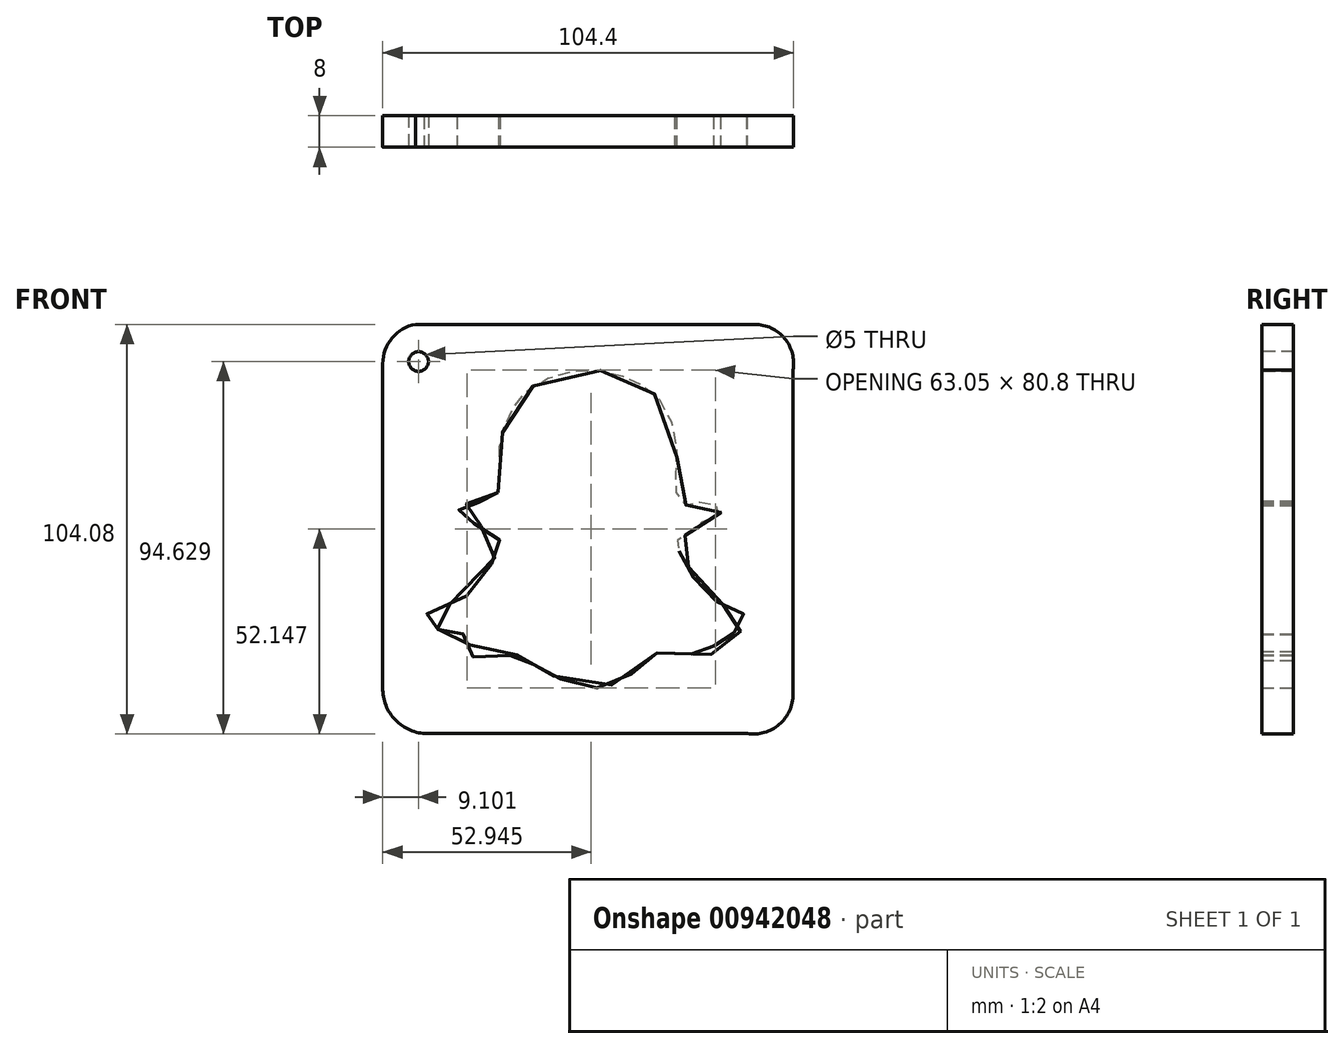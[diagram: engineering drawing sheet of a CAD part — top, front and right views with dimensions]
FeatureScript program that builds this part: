
annotation { "Feature Type Name" : "Feature", "Feature Type Description" : "" }
export const myFeature = defineFeature(function(context is Context, id is Id, definition is map)
    precondition{}
    {
        {
            var Q0;
            Q0=qCreatedBy(makeId("Front.planeOp"),FACE);
            var sketch = newSketch(context, id + "F0", { "sketchPlane" : qUnion([Q0])});
            skFitSpline(sketch, "E0", {"points": [v(-22.56, 0) * mm, v(-22.27, 10.78) * mm, v(-19.69, 19.69) * mm, v(-13.94, 26.87) * mm, v(0, 31.18) * mm, v(10.78, 28.88) * mm, v(18.83, 23.14) * mm, v(22.85, 9.63) * mm, v(22.56, 0) * mm, v(25.72, -3.3) * mm, v(30.32, -2.16) * mm, v(34.06, -5.03) * mm, v(29.17, -7.62) * mm, v(25.15, -10.78) * mm, v(22.56, -12.79) * mm, v(24.57, -16.53) * mm, v(27.73, -22.85) * mm, v(34.06, -28.3) * mm, v(39.8, -30.9) * mm, v(39.8, -34.92) * mm, v(32.62, -36.64) * mm, v(32.05, -40.67) * mm, v(24, -40.67) * mm, v(16.81, -41.24) * mm, v(10.2, -47) * mm, v(0, -49.58) * mm, v(-9.34, -46.13) * mm, v(-14.23, -43.26) * mm, v(-17.96, -41.24) * mm, v(-28.6, -42.1) * mm, v(-30.32, -36.36) * mm, v(-34.63, -36.07) * mm, v(-39.23, -33.77) * mm, v(-41.24, -31.47) * mm, v(-30.6, -26.3) * mm, v(-23.71, -17.1) * mm, v(-21.99, -12.79) * mm, v(-25.44, -9.05) * mm, v(-32.62, -6.18) * mm, v(-32.33, -4.17) * mm, v(-28.88, -2.44) * mm, v(-26.3, -2.73) * mm, v(-22.56, 0) * mm]});
            skLineSegment(sketch, "E1", {"start": v(-51.89, 32.7) * mm, "end": v(-51.89, -49.62) * mm});
            skLineSegment(sketch, "E2", {"start": v(-40.52, -61.26) * mm, "end": v(40.71, -61.26) * mm});
            skLineSegment(sketch, "E3", {"start": v(52.35, -51.24) * mm, "end": v(52.35, 31.07) * mm});
            skLineSegment(sketch, "E4", {"start": v(42.6, 42.71) * mm, "end": v(-37.27, 42.71) * mm});
            skArc(sketch, "E5", {"start": v(-51.89, -49.62) * mm, "mid": v(-48.65, -57.83) * mm, "end": v(-40.52, -61.26) * mm});
            skArc(sketch, "E6", {"start": v(52.35, 31.07) * mm, "mid": v(50.2, 39.17) * mm, "end": v(42.6, 42.71) * mm});
            skArc(sketch, "E7", {"start": v(-43.53, 42.71) * mm, "mid": v(-49.52, 39.22) * mm, "end": v(-51.89, 32.7) * mm});
            skArc(sketch, "E8", {"start": v(40.71, -61.26) * mm, "mid": v(48.83, -58.92) * mm, "end": v(52.35, -51.24) * mm});
            skLineSegment(sketch, "E9", {"start": v(-43.53, 42.71) * mm, "end": v(-37.27, 42.71) * mm});
            skSolve(sketch);
        }
        {
            var Q0;
            Q0 = qSketchRegion(id + "F0", true);
            extrude(context, id + "F1", {"entities" : qUnion([Q0]), "depth" : 8 * mm, "offsetDistance" : 25 * mm});
        }
        {
            var Q0;
            Q0=makeQuery(id+"F1.opExtrude","CAP_FACE",FACE,{"disambiguationData":[OSD([sQuery(id+"F0.wireOp",EDGE,"E0"),sQuery(id+"F0.wireOp",EDGE,"E1"),sQuery(id+"F0.wireOp",EDGE,"E2"),sQuery(id+"F0.wireOp",EDGE,"E3"),sQuery(id+"F0.wireOp",EDGE,"E4"),sQuery(id+"F0.wireOp",EDGE,"E5"),sQuery(id+"F0.wireOp",EDGE,"E6"),sQuery(id+"F0.wireOp",EDGE,"E7"),sQuery(id+"F0.wireOp",EDGE,"E8"),sQuery(id+"F0.wireOp",EDGE,"E9")])],"isStart":false});
            var sketch = newSketch(context, id + "F2", { "sketchPlane" : qUnion([Q0])});
            skCircle(sketch, "E10", {"center": v(-42.79, 33.26) * mm, "radius": 5.3 * mm});
            skPoint(sketch, "E10.first.point", {"position": v(-44.6, 38.24) * mm});
            skPoint(sketch, "E10.second.point", {"position": v(-43.73, 28.04) * mm});
            skPoint(sketch, "E10.third.point", {"position": v(-46.8, 36.71) * mm});
            skSolve(sketch);
        }
        {
            var Q0;
            Q0=sQuery(id+"F2.wireOp",VERTEX,"E10.center");
            var Q1;
            Q1=makeQuery(id+"F1.opExtrude","SWEPT_BODY",BODY,{"disambiguationData":[OSD([sQuery(id+"F0.wireOp",EDGE,"E0"),sQuery(id+"F0.wireOp",EDGE,"E1"),sQuery(id+"F0.wireOp",EDGE,"E2"),sQuery(id+"F0.wireOp",EDGE,"E3"),sQuery(id+"F0.wireOp",EDGE,"E4"),sQuery(id+"F0.wireOp",EDGE,"E5"),sQuery(id+"F0.wireOp",EDGE,"E6"),sQuery(id+"F0.wireOp",EDGE,"E7"),sQuery(id+"F0.wireOp",EDGE,"E8"),sQuery(id+"F0.wireOp",EDGE,"E9")])]});
            hole(context, id + "F3", {"style" : HoleStyle.SIMPLE, "endStyle" : HoleEndStyle.THROUGH, "holeDiameter" : 5 * mm, "majorDiameter" : 5 * mm, "isTappedThrough" : true, "tappedDepth" : 12 * mm, "tapClearance" : 3, "locations" : qUnion([Q0]), "scope" : qUnion([Q1])});
        }
    });
